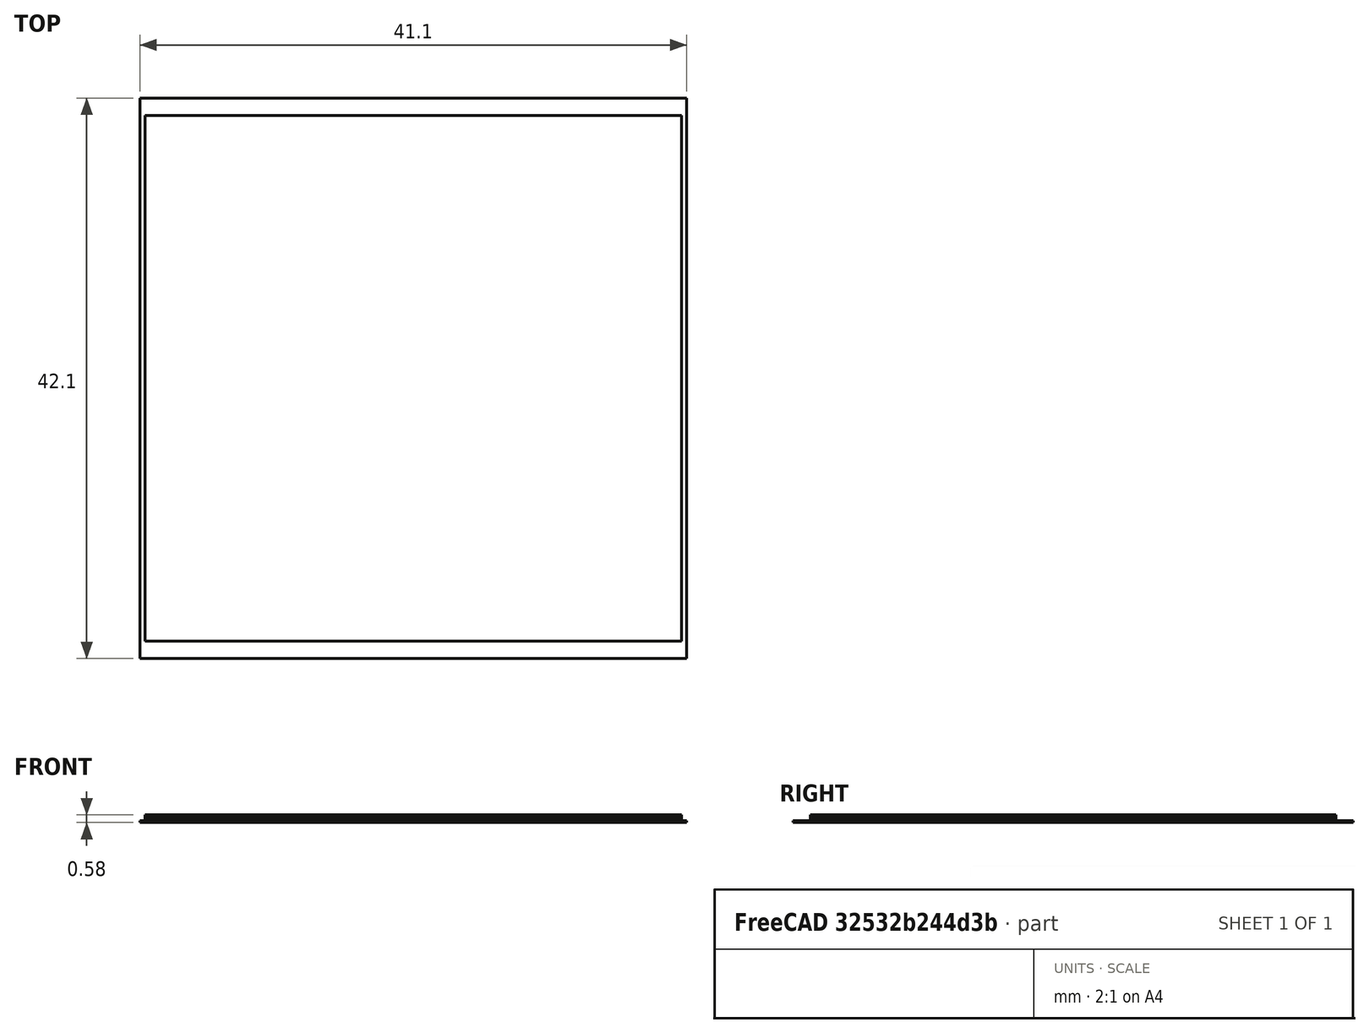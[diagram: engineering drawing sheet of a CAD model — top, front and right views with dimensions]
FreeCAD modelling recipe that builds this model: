
FCSTD DOCUMENT  (FreeCAD 0.17R13541 (Git))
Label: Liamsdesignmultibody
License: All rights reserved
LicenseURL: http://en.wikipedia.org/wiki/All_rights_reserved
objects: Sketcher::SketchObject×5, PartDesign::Pad×5, PartDesign::Body×5, PartDesign::ShapeBinder×4, App::MaterialObjectPython×4, Part::FeaturePython×2, Fem::FemMeshObjectPython×2, Fem::ConstraintInitialTemperature×1, Fem::ConstraintFixed×1, Fem::ConstraintHeatflux×1, Fem::FemSolverObjectPython×1, Fem::FemResultObjectPython×1, Fem::FemAnalysis×1
note: 26 computed .brp shape members not serialized (recipe doc carries the construction recipe); baked Part::Feature solids carry a one-line shape summary decoded from their .brp

FEATURE [Sketcher::SketchObject] Sketch
  MapMode = 5
  Support = -> [XY_Plane]
  sketch-geometry (4):
    g0: LineSegment StartX=0 StartY=0 StartZ=0 EndX=41.1 EndY=0 EndZ=0
    g1: LineSegment StartX=41.1 StartY=0 StartZ=0 EndX=41.1 EndY=42.1 EndZ=0
    g2: LineSegment StartX=41.1 StartY=42.1 StartZ=0 EndX=0 EndY=42.1 EndZ=0
    g3: LineSegment StartX=0 StartY=42.1 StartZ=0 EndX=0 EndY=0 EndZ=0
  constraints (11):
    c: Coincident(g0,g1)
    c: Coincident(g1,g2)
    c: Coincident(g2,g3)
    c: Coincident(g3,g0)
    c: Horizontal(g0)
    c: Horizontal(g2)
    c: Vertical(g1)
    c: Vertical(g3)
    c: Coincident(g0,g-1)
    c: DistanceX(g2,g2) = 41.1
    c: DistanceY(g3,g3) = 42.1
FEATURE [PartDesign::Pad] Pad
  Length = 0.15
  Length2 = 100
  Profile = -> Sketch
  Type = 0
FEATURE [PartDesign::Body] Body
  Group = -> [Sketch,Pad]
  Origin = -> Origin
  Tip = -> Pad
FEATURE [PartDesign::ShapeBinder] CopyPad
  Placement = pos=(0,0,0.15) rot=(0,0,1;0rad)
FEATURE [Sketcher::SketchObject] Sketch001
  MapMode = 5
  Placement = pos=(0,0,0.15) rot=(0,0,1;0rad)
  Support = -> [CopyPad]
  sketch-geometry (4):
    g0: LineSegment StartX=0.4 StartY=1.3 StartZ=0 EndX=40.7 EndY=1.3 EndZ=0
    g1: LineSegment StartX=40.7 StartY=1.3 StartZ=0 EndX=40.7 EndY=40.8 EndZ=0
    g2: LineSegment StartX=40.7 StartY=40.8 StartZ=0 EndX=0.4 EndY=40.8 EndZ=0
    g3: LineSegment StartX=0.4 StartY=40.8 StartZ=0 EndX=0.4 EndY=1.3 EndZ=0
  constraints (12):
    c: Coincident(g0,g1)
    c: Coincident(g1,g2)
    c: Coincident(g2,g3)
    c: Coincident(g3,g0)
    c: Horizontal(g0)
    c: Horizontal(g2)
    c: Vertical(g1)
    c: Vertical(g3)
    c: DistanceX(g2,g2) = 40.3
    c: DistanceY(g3,g3) = 39.5
    c: DistanceY(g-1,g0) = 1.3
    c: DistanceX(g-1,g0) = 0.4
FEATURE [PartDesign::Pad] Pad001
  Length = 0.025
  Length2 = 100
  Placement = pos=(0,0,0.15) rot=(0,0,1;0rad)
  Profile = -> Sketch001
  Type = 0
FEATURE [PartDesign::Body] Body001
  Group = -> [CopyPad,Sketch001,Pad001]
  Origin = -> Origin001
  Tip = -> Pad001
FEATURE [PartDesign::ShapeBinder] CopyPad001
  Placement = pos=(0,0,0.025) rot=(0,0,1;0rad)
FEATURE [Sketcher::SketchObject] Sketch002
  ExternalGeometry = -> [CopyPad001]
  MapMode = 5
  Placement = pos=(0,0,0.175) rot=(0,0,1;0rad)
  Support = -> [CopyPad001]
  sketch-geometry (4):
    g0: LineSegment StartX=0.4 StartY=1.3 StartZ=0 EndX=40.7 EndY=1.3 EndZ=0
    g1: LineSegment StartX=40.7 StartY=1.3 StartZ=0 EndX=40.7 EndY=40.8 EndZ=0
    g2: LineSegment StartX=40.7 StartY=40.8 StartZ=0 EndX=0.4 EndY=40.8 EndZ=0
    g3: LineSegment StartX=0.4 StartY=40.8 StartZ=0 EndX=0.4 EndY=1.3 EndZ=0
  constraints (10):
    c: Coincident(g0,g1)
    c: Coincident(g1,g2)
    c: Coincident(g2,g3)
    c: Coincident(g3,g0)
    c: Horizontal(g0)
    c: Horizontal(g2)
    c: Vertical(g1)
    c: Vertical(g3)
    c: Coincident(g0,g-4)
    c: Coincident(g1,g-3)
FEATURE [PartDesign::Pad] Pad002
  Length = 0.15
  Length2 = 100
  Placement = pos=(0,0,0.025) rot=(0,0,1;0rad)
  Profile = -> Sketch002
  Type = 0
FEATURE [PartDesign::Body] Body002
  Group = -> [CopyPad001,Sketch002,Pad002]
  Origin = -> Origin002
  Tip = -> Pad002
FEATURE [PartDesign::ShapeBinder] CopyPad002
  Placement = pos=(0,0,0.15) rot=(0,0,1;0rad)
FEATURE [Sketcher::SketchObject] Sketch003
  MapMode = 5
  Placement = pos=(0,0,0.325) rot=(0,0,1;0rad)
  Support = -> [CopyPad002]
  sketch-geometry (4):
    g0: LineSegment StartX=0.4 StartY=40.8 StartZ=0 EndX=40.7 EndY=40.8 EndZ=0
    g1: LineSegment StartX=40.7 StartY=40.8 StartZ=0 EndX=40.7 EndY=1.3 EndZ=0
    g2: LineSegment StartX=40.7 StartY=1.3 StartZ=0 EndX=0.4 EndY=1.3 EndZ=0
    g3: LineSegment StartX=0.4 StartY=1.3 StartZ=0 EndX=0.4 EndY=40.8 EndZ=0
  constraints (12):
    c: Coincident(g0,g1)
    c: Coincident(g1,g2)
    c: Coincident(g2,g3)
    c: Coincident(g3,g0)
    c: Horizontal(g0)
    c: Horizontal(g2)
    c: Vertical(g1)
    c: Vertical(g3)
    c: DistanceY(g-1,g2) = 1.3
    c: DistanceX(g-1,g2) = 0.4
    c: DistanceX(g0,g0) = 40.3
    c: DistanceY(g3,g3) = 39.5
FEATURE [PartDesign::Pad] Pad003
  Length = 0.05
  Length2 = 100
  Placement = pos=(0,0,0.15) rot=(0,0,1;0rad)
  Profile = -> Sketch003
  Type = 0
FEATURE [PartDesign::Body] Body003
  Group = -> [CopyPad002,Sketch003,Pad003]
  Origin = -> Origin003
  Tip = -> Pad003
FEATURE [PartDesign::ShapeBinder] CopyPad003
  Placement = pos=(0,0,0.05) rot=(0,0,1;0rad)
FEATURE [Sketcher::SketchObject] Sketch004
  MapMode = 5
  Placement = pos=(0,0,0.375) rot=(0,0,1;0rad)
  Support = -> [CopyPad003]
  sketch-geometry (4):
    g0: LineSegment StartX=0.4 StartY=40.8 StartZ=0 EndX=40.7 EndY=40.8 EndZ=0
    g1: LineSegment StartX=40.7 StartY=40.8 StartZ=0 EndX=40.7 EndY=1.3 EndZ=0
    g2: LineSegment StartX=40.7 StartY=1.3 StartZ=0 EndX=0.4 EndY=1.3 EndZ=0
    g3: LineSegment StartX=0.4 StartY=1.3 StartZ=0 EndX=0.4 EndY=40.8 EndZ=0
  constraints (12):
    c: Coincident(g0,g1)
    c: Coincident(g1,g2)
    c: Coincident(g2,g3)
    c: Coincident(g3,g0)
    c: Horizontal(g0)
    c: Horizontal(g2)
    c: Vertical(g1)
    c: Vertical(g3)
    c: DistanceX(g-1,g2) = 0.4
    c: DistanceY(g-1,g2) = 1.3
    c: DistanceX(g0,g0) = 40.3
    c: DistanceY(g3,g3) = 39.5
FEATURE [PartDesign::Pad] Pad004
  Length = 0.21
  Length2 = 100
  Placement = pos=(0,0,0.05) rot=(0,0,1;0rad)
  Profile = -> Sketch004
  Type = 0
FEATURE [PartDesign::Body] Body004
  Group = -> [CopyPad003,Sketch004,Pad004]
  Origin = -> Origin004
  Tip = -> Pad004
FEATURE [Fem::ConstraintInitialTemperature] FemConstraintInitialTemperature
  NormalDirection = (0,0,1)
  initialTemperature = 300
FEATURE [Fem::ConstraintFixed] FemConstraintFixed
  NormalDirection = (0,0,-1)
  Normals = (16) [(0,0,-1),(0,0,-1),(0,0,-1),(0,0,-1),(0,0,-1),(0,0,-1),(0,0,-1),(0,0,-1),(0,0,-1),(0,0,-1),(0,0,-1),(0,0,-1),(0,0,-1),(0,0,-1),(0,0,-1),(0,0,-1)]
  Points = (16) [(0,0,0),(13.7,0,0),(27.4,0,0),(41.1,0,0),(0,14.0333,0),(13.7,14.0333,0),(27.4,14.0333,0),(41.1,14.0333,0),(0,28.0667,0),(13.7,28.0667,0),+6 more]
  References = -> [Pad]
  Scale = 5
FEATURE [Fem::ConstraintHeatflux] FemConstraintHeatflux
  AmbientTemp = 213
  ConstraintType = 1
  DFlux = 0
  FilmCoef = 10
  NormalDirection = (0,0,-1)
  Normals = (272) [(0,0,-1),(0,0,-1),(0,0,-1),(0,0,-1),(0,0,-1),(0,0,-1),(0,0,-1),(0,0,-1),(0,0,-1),(0,0,-1),(0,0,-1),(0,0,-1),(0,0,-1),(0,0,-1),(0,0,-1),(0,0,-1),+256 more]
  Points = (272) [(0,0,0),(13.7,0,0),(27.4,0,0),(41.1,0,0),(0,14.0333,0),(13.7,14.0333,0),(27.4,14.0333,0),(41.1,14.0333,0),(0,28.0667,0),(13.7,28.0667,0),+262 more]
  References = -> [Pad,Pad001,Pad002,Pad003,Pad004]
  Scale = 3
FEATURE [Part::FeaturePython] BooleanFragments  # WARN: FeaturePython — macro-defined, semantics opaque (R4)
  Mode = 2
  Objects = -> [Body,Body001,Body002,Body003,Body004]
  Tolerance = 0
FEATURE [Part::FeaturePython] CompoundFilter  # WARN: FeaturePython — macro-defined, semantics opaque (R4)
  Base = -> BooleanFragments
  FilterType = 3
  Invert = false
  OverrideMaxVal = 0
  WindowFrom = 80
  WindowTo = 100
FEATURE [App::MaterialObjectPython] SolidMaterial  # material (typed FeaturePython)
  Category = 0
  Material = Density=1420.0 kg/m^3,Description=This is a not defined material,Father=None,Name=None,PoissonRatio=0.34,SpecificHeat=1.09 J/kg/K,SpecificPrice=0,+4 more (map truncated)
  References = -> [CompoundFilter]
FEATURE [App::MaterialObjectPython] SolidMaterial001  # material (typed FeaturePython)
  Category = 0
  Material = Density=1000.0 kg/m^3,Description=This is a not defined material,Father=None,Name=None,PoissonRatio=0.35,SpecificHeat=0.8 J/kg/K,SpecificPrice=0,+4 more (map truncated)
  References = -> [CompoundFilter]
FEATURE [App::MaterialObjectPython] SolidMaterial002  # material (typed FeaturePython)
  Category = 0
  Material = Density=2329.0 kg/m^3,Description=This is a not defined material,Father=None,Name=None,PoissonRatio=0.28,SpecificHeat=0.71 J/kg/K,SpecificPrice=0,+4 more (map truncated)
  References = -> [CompoundFilter]
FEATURE [App::MaterialObjectPython] SolidMaterial003  # material (typed FeaturePython)
  Category = 0
  Material = Density=2698.9 kg/m^3,Description=This is a not defined material,Father=None,Name=None,PoissonRatio=0.36,SpecificHeat=0.9 J/kg/K,SpecificPrice=0,+4 more (map truncated)
  References = -> [CompoundFilter]
FEATURE [Fem::FemMeshObjectPython] FEMMeshGmsh  # FEM object (typed FeaturePython)
  Algorithm2D = 0
  Algorithm3D = 0
  CharacteristicLengthMax = 0
  CharacteristicLengthMin = 0
  CoherenceMesh = true
  ElementDimension = 3
  ElementOrder = 1
  GeometryTolerance = 1e-06
  GroupsOfNodes = false
  HighOrderOptimize = false
  OptimizeNetgen = false
  OptimizeStd = true
  Part = -> CompoundFilter
  RecombineAll = false
FEATURE [Fem::FemSolverObjectPython] CalculiXccxTools  # FEM object (typed FeaturePython)
  AnalysisType = 2
  BeamShellResultOutput3D = false
  EigenmodeHighLimit = 1000000
  EigenmodeLowLimit = 0
  EigenmodesCount = 10
  GeometricalNonlinearity = 0
  IterationsControlParameterCutb = 0.25,0.5,0.75,0.85,,,1.5,
  IterationsControlParameterIter = 4,8,9,200,10,400,,200,,
  IterationsControlParameterTimeUse = false
  IterationsThermoMechMaximum = 2000
  IterationsUserDefinedIncrementations = false
  IterationsUserDefinedTimeStepLength = false
  MaterialNonlinearity = 0
  MatrixSolverType = 0
  SplitInputWriter = false
  ThermoMechSteadyState = true
  TimeEnd = 1
  TimeInitialStep = 1
FEATURE [Fem::FemMeshObjectPython] Result_mesh  # FEM object (typed FeaturePython)
FEATURE [Fem::FemResultObjectPython] CalculiX_thermomech_results  # FEM object (typed FeaturePython)
  DisplacementLengths = [0,5.28568e-05,0,5.33697e-05,0,5.34275e-05,0,5.31766e-05,5.94516e-05,6.01928e-05,5.9995e-05,6.0103e-05,0.000168439,0.000168863,0.000168541,0.000168388,0.000226059,0.000225939,0.000225922,0.000225363,0.00171326,0.00168438,0.00169232,+4277 more]
  DisplacementVectors = (4300) [(0,0,0),(2.12016e-05,2.69702e-05,-4.02112e-05),(0,0,0),(-2.11538e-05,2.83629e-05,-3.99548e-05),(0,0,0),(2.12635e-05,-2.83561e-05,-3.99786e-05),+4294 more]
  Eigenmode = 0
  EigenmodeFrequency = 0
  MaxShear = [27.8918,19.1046,28.4008,18.6143,28.4705,18.6266,28.2362,19.1207,50.0617,43.3726,53.3497,53.0061,62.0787,71.8078,54.2831,45.6926,21.3552,21.1125,19.7464,20.3254,24.4571,24.2342,21.837,22.2931,25.5248,25.0819,25.4867,25.2349,22.798,22.3553,+4270 more]
  Mesh = -> Result_mesh
  NodeNumbers = [1,2,3,4,5,6,7,8,9,10,11,12,13,14,15,16,17,18,19,20,21,22,23,24,25,26,27,28,29,30,31,32,33,34,35,36,37,38,39,40,41,42,43,44,45,46,47,48,49,50,51,52,53,54,55,56,57,58,59,60,61,62,63,64,65,66,67,68,69,+4231 more]
  PrincipalMax = [52.8711,35.9927,54.7631,34.8847,54.873,34.9185,53.5724,36.0997,97.613,83.4402,104.419,102.843,122.417,141.83,105.697,87.6573,35.5783,35.1709,33.0064,33.7,43.7143,44.1271,38.7502,40.438,49.9332,50.1987,49.7887,50.5036,41.1831,39.7486,+4270 more]
  PrincipalMed = [46.6105,25.8232,42.4793,25.4954,42.5196,25.5829,46.9626,26.2321,92.081,74.7241,98.9242,95.1174,115.841,137.573,97.7875,81.4402,26.8443,26.3927,25.4193,24.9808,35.8451,36.7688,31.4019,34.9933,46.6611,44.9648,44.6056,47.2366,38.0253,37.3484,+4270 more]
  PrincipalMin = [-2.91244,-2.21646,-2.03862,-2.344,-2.06808,-2.33457,-2.89993,-2.14164,-2.51044,-3.30506,-2.28,-3.16962,-1.74058,-1.78601,-2.86911,-3.72791,-7.13214,-7.05416,-6.48634,-6.95074,-5.19982,-4.34142,-4.92374,-4.14826,-1.11628,0.0349405,-1.18481,+4273 more]
  ResultType = Fem::FemResultMechanical
  Stats = [-0.00186393,1.36874e-07,0.00184983,-0.00181854,-1.4375e-07,0.00177321,-0.00169888,-0.000426062,0,0,0.000495664,0.00236136,21.3719,73.9651,224.933,20.1133,74.5241,230.142,-5.97491,68.7498,223.257,-11.1076,-1.39053,3.13297,10.6873,37.9573,+13 more]
  StrainVectors = (4300) [(-9.29617e-06,-3.4841e-06,-0.000283202),(-7.31419e-05,-3.4162e-05,-0.000275203),(-4.26758e-05,-3.89244e-06,-0.000252609),+4297 more]
  StressValues = [52.9317,34.2752,51.7647,33.5348,51.8795,33.5733,53.4747,34.3863,97.4752,82.7323,104.061,102.368,121.004,141.535,104.835,88.4407,39.0824,38.5921,36.2988,37.0684,45.4929,45.2404,40.5029,42.1286,49.4947,47.7624,48.5897,48.9181,44.1019,43.56,+4270 more]
  StressVectors = (4300) [(45.3151,46.1688,5.08527),(27.8507,33.5758,-1.82702),(40.1138,45.8101,9.27982),(27.5045,32.5751,-2.04348),(40.1738,45.8412,9.30956),+4295 more]
  Time = 1
FEATURE [Fem::FemAnalysis] Analysis
  Group = -> [FemConstraintInitialTemperature,FemConstraintFixed,FemConstraintHeatflux,SolidMaterial,SolidMaterial001,SolidMaterial002,SolidMaterial003,FEMMeshGmsh,CalculiXccxTools,CalculiX_thermomech_results]
